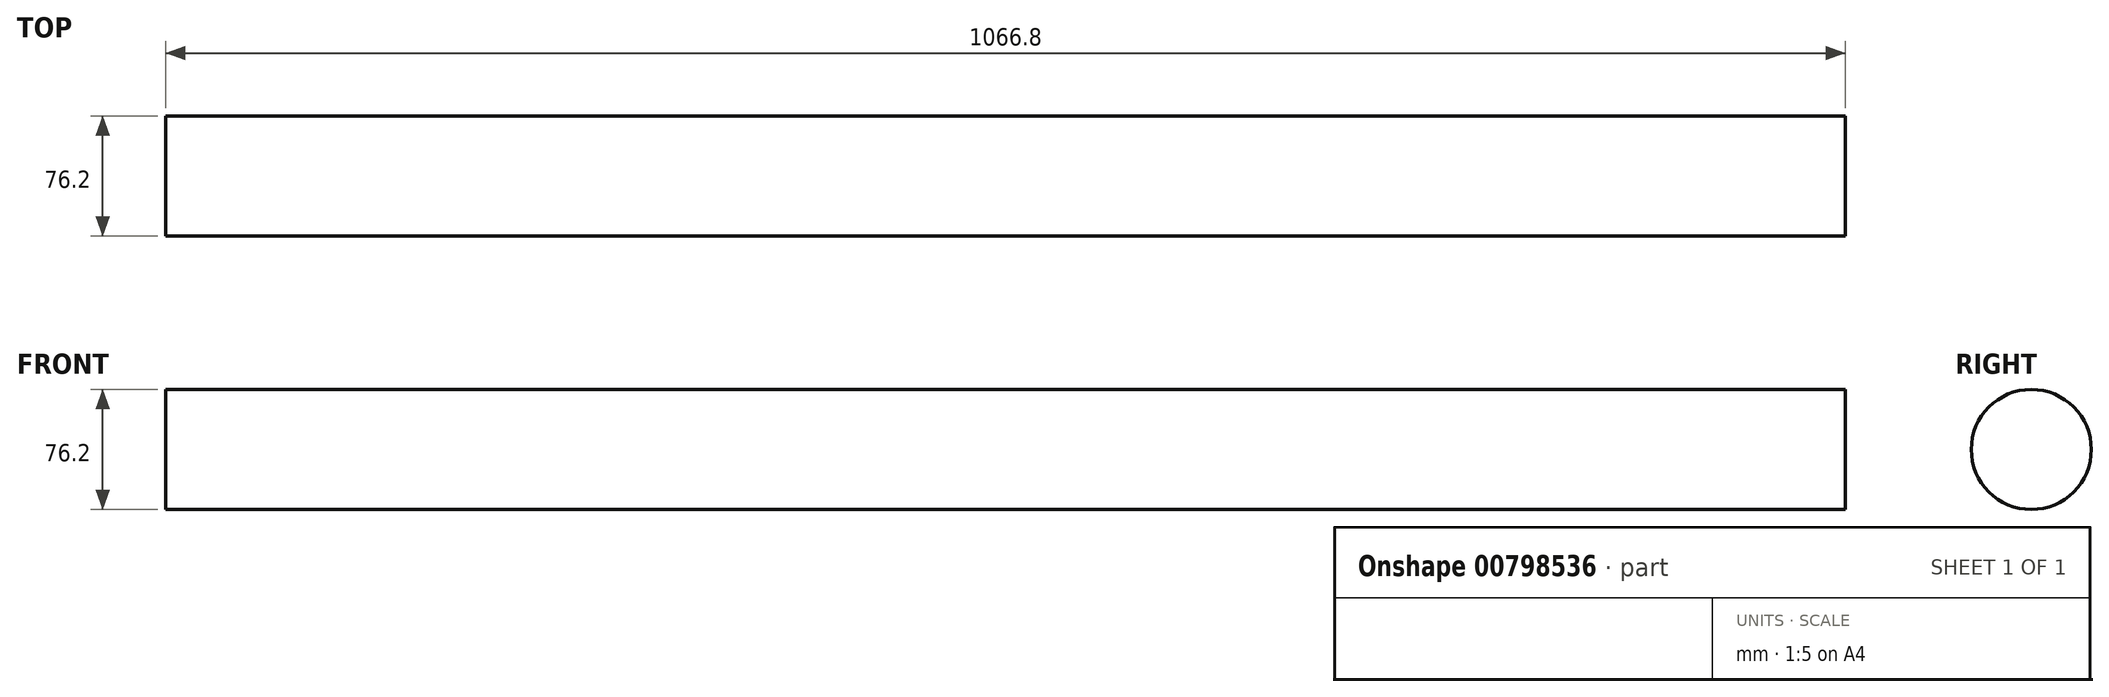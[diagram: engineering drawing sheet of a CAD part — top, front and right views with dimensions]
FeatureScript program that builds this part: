
annotation { "Feature Type Name" : "Feature", "Feature Type Description" : "" }
export const myFeature = defineFeature(function(context is Context, id is Id, definition is map)
    precondition{}
    {
        {
            var Q0;
            Q0=qCreatedBy(makeId("Right.planeOp"),FACE);
            var sketch = newSketch(context, id + "F0", { "sketchPlane" : qUnion([Q0])});
            skCircle(sketch, "E0", {"center": v(0, 0) * mm, "radius": 38.1 * mm});
            skSolve(sketch);
        }
        {
            var Q0;
            Q0 = qSketchRegion(id + "F0", true);
            extrude(context, id + "F1", {"entities" : qUnion([Q0]), "depth" : 1066.8 * mm, "offsetDistance" : 30.48 * mm});
        }
    });
